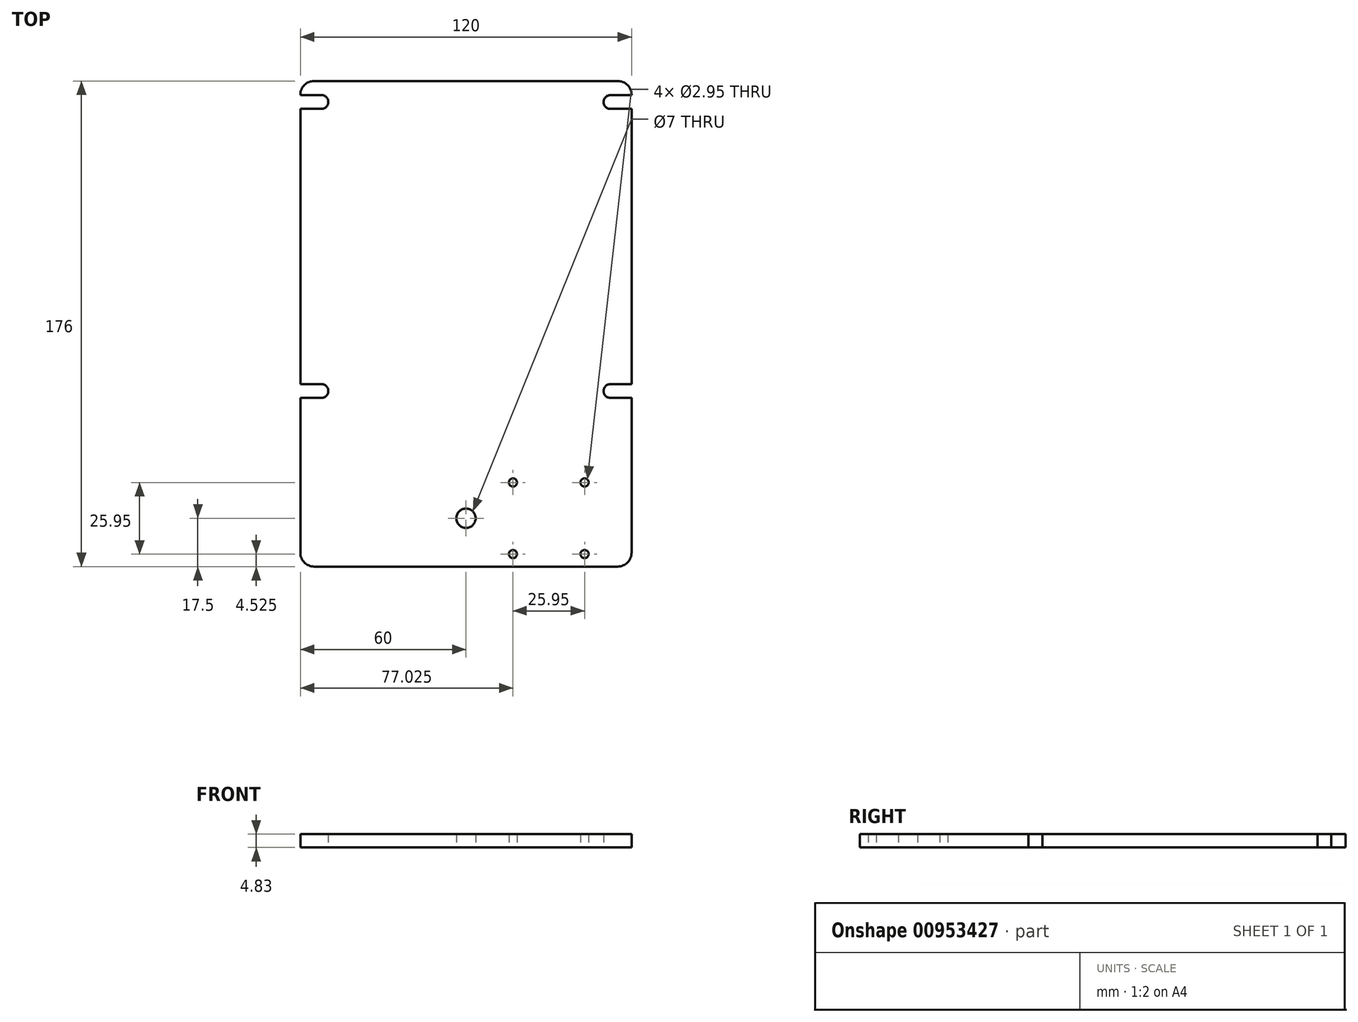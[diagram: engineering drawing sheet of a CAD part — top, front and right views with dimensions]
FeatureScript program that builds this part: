
annotation { "Feature Type Name" : "Feature", "Feature Type Description" : "" }
export const myFeature = defineFeature(function(context is Context, id is Id, definition is map)
    precondition{}
    {
        {
            var Q0;
            Q0=qCreatedBy(makeId("Top.planeOp"),FACE);
            var sketch = newSketch(context, id + "F0", { "sketchPlane" : qUnion([Q0])});
            skLineSegment(sketch, "E0.bottom", {"start": v(60, -60) * mm, "end": v(-60, -60) * mm, "construction": true});
            skLineSegment(sketch, "E0.top", {"start": v(60, 60) * mm, "end": v(-60, 60) * mm});
            skLineSegment(sketch, "E0.left", {"start": v(60, -60) * mm, "end": v(60, 60) * mm});
            skLineSegment(sketch, "E0.right", {"start": v(-60, -60) * mm, "end": v(-60, 60) * mm});
            skPoint(sketch, "E0.middle", {"position": v(0, 0) * mm});
            skLineSegment(sketch, "E1", {"start": v(-60, 60) * mm, "end": v(60, -60) * mm, "construction": true});
            skCircle(sketch, "E2", {"center": v(-52.37, 52.37) * mm, "radius": 2 * mm});
            skLineSegment(sketch, "E3", {"start": v(-52.37, 54.37) * mm, "end": v(-52.37, 50.38) * mm, "construction": true});
            skLineSegment(sketch, "E4", {"start": v(-54.37, 52.37) * mm, "end": v(-50.37, 52.37) * mm, "construction": true});
            skCircle(sketch, "E5.1.0", {"center": v(-52.37, -52.37) * mm, "radius": 2 * mm});
            skLineSegment(sketch, "E5.1.1", {"start": v(-52.37, -54.37) * mm, "end": v(-52.37, -50.37) * mm, "construction": true});
            skLineSegment(sketch, "E5.1.2", {"start": v(-54.37, -52.37) * mm, "end": v(-50.38, -52.37) * mm, "construction": true});
            skCircle(sketch, "E5.2.0", {"center": v(52.37, -52.37) * mm, "radius": 2 * mm});
            skLineSegment(sketch, "E5.2.1", {"start": v(54.37, -52.37) * mm, "end": v(50.37, -52.37) * mm, "construction": true});
            skLineSegment(sketch, "E5.2.2", {"start": v(52.37, -54.37) * mm, "end": v(52.37, -50.38) * mm, "construction": true});
            skCircle(sketch, "E5.3.0", {"center": v(52.37, 52.37) * mm, "radius": 2 * mm});
            skLineSegment(sketch, "E5.3.1", {"start": v(52.37, 54.37) * mm, "end": v(52.37, 50.37) * mm, "construction": true});
            skLineSegment(sketch, "E5.3.2", {"start": v(54.37, 52.37) * mm, "end": v(50.38, 52.37) * mm, "construction": true});
            skLineSegment(sketch, "E6", {"start": v(60, -75) * mm, "end": v(-60, -75) * mm, "construction": true});
            skLineSegment(sketch, "E7", {"start": v(60, -81) * mm, "end": v(-60, -81) * mm, "construction": true});
            skLineSegment(sketch, "E8", {"start": v(-60, -116) * mm, "end": v(60, -116) * mm, "construction": true});
            skLineSegment(sketch, "E9", {"start": v(-60, -60) * mm, "end": v(-60, -116) * mm});
            skLineSegment(sketch, "E10", {"start": v(-60, -116) * mm, "end": v(60, -116) * mm});
            skLineSegment(sketch, "E11", {"start": v(60, -116) * mm, "end": v(60, -60) * mm});
            skCircle(sketch, "E12", {"center": v(0, 0) * mm, "radius": 19.75 * mm, "construction": true});
            skCircle(sketch, "E13", {"center": v(0, 0) * mm, "radius": 58.1 * mm, "construction": true});
            skSolve(sketch);
        }
        {
            var Q0;
            Q0=makeQuery(id+"F0.imprint","IMPRINT",FACE,{"disambiguationData":[TD([[makeQuery(id+"F0.imprint","IMPRINT",EDGE,{"derivedFrom":sQuery(id+"F0.wireOp",EDGE,"E0.top")}),1.0]])]});
            var sketch = newSketch(context, id + "F1", { "sketchPlane" : qUnion([Q0])});
            skLineSegment(sketch, "E14.0", {"start": v(60, 60) * mm, "end": v(-60, 60) * mm});
            skLineSegment(sketch, "E15.0", {"start": v(-60, -60) * mm, "end": v(-60, 60) * mm});
            skLineSegment(sketch, "E16.0", {"start": v(60, -60) * mm, "end": v(60, 60) * mm});
            skLineSegment(sketch, "E17.0", {"start": v(60, -116) * mm, "end": v(60, -60) * mm});
            skLineSegment(sketch, "E18.0", {"start": v(-60, -60) * mm, "end": v(-60, -116) * mm});
            skLineSegment(sketch, "E19.0", {"start": v(-60, -116) * mm, "end": v(60, -116) * mm});
            skLineSegment(sketch, "E20.0", {"start": v(60, -81) * mm, "end": v(-60, -81) * mm, "construction": true});
            skCircle(sketch, "E21.0", {"center": v(52.37, -52.37) * mm, "radius": 2 * mm, "construction": true});
            skCircle(sketch, "E22.0", {"center": v(-52.37, -52.37) * mm, "radius": 2 * mm, "construction": true});
            skCircle(sketch, "E23.0", {"center": v(52.37, 52.37) * mm, "radius": 2 * mm, "construction": true});
            skCircle(sketch, "E24.0", {"center": v(-52.37, 52.37) * mm, "radius": 2 * mm, "construction": true});
            skLineSegment(sketch, "E25.bottom", {"start": v(-14, -114.5) * mm, "end": v(-46, -114.5) * mm, "construction": true});
            skLineSegment(sketch, "E25.top", {"start": v(-14, -82.5) * mm, "end": v(-46, -82.5) * mm, "construction": true});
            skLineSegment(sketch, "E25.left", {"start": v(-14, -114.5) * mm, "end": v(-14, -82.5) * mm, "construction": true});
            skLineSegment(sketch, "E25.right", {"start": v(-46, -114.5) * mm, "end": v(-46, -82.5) * mm, "construction": true});
            skPoint(sketch, "E25.middle", {"position": v(-30, -98.5) * mm});
            skCircle(sketch, "E26", {"center": v(0, -98.5) * mm, "radius": 3.5 * mm});
            skLineSegment(sketch, "E27", {"start": v(0, -81) * mm, "end": v(0, -98.5) * mm, "construction": true});
            skLineSegment(sketch, "E28", {"start": v(0, -98.5) * mm, "end": v(0, -116) * mm, "construction": true});
            skLineSegment(sketch, "E29", {"start": v(0, -98.5) * mm, "end": v(-30, -98.5) * mm, "construction": true});
            skLineSegment(sketch, "E30", {"start": v(-30, -98.5) * mm, "end": v(-60, -98.5) * mm, "construction": true});
            skLineSegment(sketch, "E31.bottom", {"start": v(5.62, -103.25) * mm, "end": v(-5.63, -103.25) * mm, "construction": true});
            skLineSegment(sketch, "E31.top", {"start": v(5.62, -93.75) * mm, "end": v(-5.62, -93.75) * mm, "construction": true});
            skLineSegment(sketch, "E31.left", {"start": v(5.62, -103.25) * mm, "end": v(5.62, -93.75) * mm, "construction": true});
            skLineSegment(sketch, "E31.right", {"start": v(-5.63, -103.25) * mm, "end": v(-5.62, -93.75) * mm, "construction": true});
            skLineSegment(sketch, "E32", {"start": v(-14, -114.5) * mm, "end": v(-46, -82.5) * mm, "construction": true});
            skCircle(sketch, "E33", {"center": v(-42.98, -85.53) * mm, "radius": 1.43 * mm, "construction": true});
            skLineSegment(sketch, "E34", {"start": v(-41.55, -85.53) * mm, "end": v(-44.4, -85.53) * mm, "construction": true});
            skLineSegment(sketch, "E35", {"start": v(-42.98, -84.1) * mm, "end": v(-42.98, -86.95) * mm, "construction": true});
            skLineSegment(sketch, "E36.1.0", {"start": v(-44.4, -111.47) * mm, "end": v(-41.55, -111.47) * mm, "construction": true});
            skCircle(sketch, "E36.1.1", {"center": v(-42.98, -111.47) * mm, "radius": 1.43 * mm, "construction": true});
            skLineSegment(sketch, "E36.1.2", {"start": v(-42.98, -110.05) * mm, "end": v(-42.98, -112.9) * mm, "construction": true});
            skLineSegment(sketch, "E36.2.0", {"start": v(-17.03, -112.9) * mm, "end": v(-17.03, -110.05) * mm, "construction": true});
            skCircle(sketch, "E36.2.1", {"center": v(-17.03, -111.48) * mm, "radius": 1.43 * mm, "construction": true});
            skLineSegment(sketch, "E36.2.2", {"start": v(-18.45, -111.48) * mm, "end": v(-15.6, -111.48) * mm, "construction": true});
            skLineSegment(sketch, "E36.3.0", {"start": v(-15.6, -85.52) * mm, "end": v(-18.45, -85.52) * mm, "construction": true});
            skCircle(sketch, "E36.3.1", {"center": v(-17.03, -85.52) * mm, "radius": 1.43 * mm, "construction": true});
            skLineSegment(sketch, "E36.3.2", {"start": v(-17.03, -86.95) * mm, "end": v(-17.03, -84.1) * mm, "construction": true});
            skLineSegment(sketch, "E37.MirrorCS", {"start": v(44.4, -111.47) * mm, "end": v(41.55, -111.47) * mm, "construction": true});
            skLineSegment(sketch, "E38.MirrorCS", {"start": v(14, -114.5) * mm, "end": v(46, -82.5) * mm, "construction": true});
            skLineSegment(sketch, "E39.MirrorCS", {"start": v(17.03, -86.95) * mm, "end": v(17.03, -84.1) * mm, "construction": true});
            skPoint(sketch, "E40.MirrorP", {"position": v(30, -98.5) * mm});
            skLineSegment(sketch, "E41.MirrorCS", {"start": v(14, -82.5) * mm, "end": v(46, -82.5) * mm, "construction": true});
            skCircle(sketch, "E42.MirrorC", {"center": v(42.98, -111.47) * mm, "radius": 1.43 * mm, "construction": true});
            skCircle(sketch, "E43.MirrorC", {"center": v(17.03, -111.48) * mm, "radius": 1.43 * mm, "construction": true});
            skLineSegment(sketch, "E44.MirrorCS", {"start": v(14, -114.5) * mm, "end": v(46, -114.5) * mm, "construction": true});
            skCircle(sketch, "E45.MirrorC", {"center": v(42.98, -85.53) * mm, "radius": 1.43 * mm, "construction": true});
            skLineSegment(sketch, "E46.MirrorCS", {"start": v(18.45, -111.48) * mm, "end": v(15.6, -111.48) * mm, "construction": true});
            skLineSegment(sketch, "E47.MirrorCS", {"start": v(42.98, -110.05) * mm, "end": v(42.98, -112.9) * mm, "construction": true});
            skLineSegment(sketch, "E48.MirrorCS", {"start": v(46, -114.5) * mm, "end": v(46, -82.5) * mm, "construction": true});
            skLineSegment(sketch, "E49.MirrorCS", {"start": v(41.55, -85.53) * mm, "end": v(44.4, -85.53) * mm, "construction": true});
            skLineSegment(sketch, "E50.MirrorCS", {"start": v(14, -114.5) * mm, "end": v(14, -82.5) * mm, "construction": true});
            skLineSegment(sketch, "E51.MirrorCS", {"start": v(15.6, -85.52) * mm, "end": v(18.45, -85.52) * mm, "construction": true});
            skLineSegment(sketch, "E52.MirrorCS", {"start": v(17.03, -112.9) * mm, "end": v(17.03, -110.05) * mm, "construction": true});
            skLineSegment(sketch, "E53.MirrorCS", {"start": v(42.98, -84.1) * mm, "end": v(42.98, -86.95) * mm, "construction": true});
            skCircle(sketch, "E54.MirrorC", {"center": v(17.03, -85.52) * mm, "radius": 1.43 * mm, "construction": true});
            skCircle(sketch, "E55", {"center": v(42.98, -85.53) * mm, "radius": 1.47 * mm});
            skCircle(sketch, "E56.1.0", {"center": v(17.03, -85.53) * mm, "radius": 1.47 * mm});
            skCircle(sketch, "E56.2.0", {"center": v(17.03, -111.48) * mm, "radius": 1.47 * mm});
            skCircle(sketch, "E56.3.0", {"center": v(42.98, -111.48) * mm, "radius": 1.47 * mm});
            skCircle(sketch, "E57", {"center": v(-52.37, 52.37) * mm, "radius": 2.5 * mm});
            skLineSegment(sketch, "E58", {"start": v(-52.37, 54.87) * mm, "end": v(-60, 54.87) * mm});
            skLineSegment(sketch, "E59", {"start": v(-52.37, 49.87) * mm, "end": v(-60, 49.87) * mm});
            skLineSegment(sketch, "E60.MirrorCS", {"start": v(52.37, 54.87) * mm, "end": v(60, 54.87) * mm});
            skLineSegment(sketch, "E61.MirrorCS", {"start": v(52.37, 49.87) * mm, "end": v(60, 49.87) * mm});
            skCircle(sketch, "E62.MirrorC", {"center": v(52.37, 52.37) * mm, "radius": 2.5 * mm});
            skLineSegment(sketch, "E63.MirrorCS", {"start": v(52.37, -54.87) * mm, "end": v(60, -54.87) * mm});
            skCircle(sketch, "E64.MirrorC", {"center": v(-52.37, -52.37) * mm, "radius": 2.5 * mm});
            skCircle(sketch, "E65.MirrorC", {"center": v(52.37, -52.37) * mm, "radius": 2.5 * mm});
            skLineSegment(sketch, "E66.MirrorCS", {"start": v(-52.37, -49.87) * mm, "end": v(-60, -49.87) * mm});
            skLineSegment(sketch, "E67.MirrorCS", {"start": v(52.37, -49.87) * mm, "end": v(60, -49.87) * mm});
            skLineSegment(sketch, "E68.MirrorCS", {"start": v(-52.37, -54.87) * mm, "end": v(-60, -54.87) * mm});
            skSolve(sketch);
        }
        {
            var Q0;
            {var subQ11=sQuery(id+"F1.wireOp",EDGE,"E14.0");Q0=makeQuery(id+"F1.imprint","IMPRINT",FACE,{"disambiguationData":[TD([[makeQuery(id+"F1.imprint","IMPRINT",EDGE,{"derivedFrom":subQ11}),1.0]])]});}
            extrude(context, id + "F2", {"entities" : qUnion([Q0]), "depth" : 4.83 * mm, "offsetDistance" : 25.4 * mm});
        }
        {
            var Q0;
            Q0=makeQuery(id+"F2.opExtrude","SWEPT_EDGE",EDGE,{"disambiguationData":[OSD([sQuery(id+"F1.wireOp",EDGE,"E14.0"),sQuery(id+"F1.wireOp",EDGE,"E15.0")])]});
            var Q1;
            Q1=makeQuery(id+"F2.opExtrude","SWEPT_EDGE",EDGE,{"disambiguationData":[OSD([sQuery(id+"F1.wireOp",EDGE,"E14.0"),sQuery(id+"F1.wireOp",EDGE,"E16.0")])]});
            var Q2;
            Q2=makeQuery(id+"F2.opExtrude","SWEPT_EDGE",EDGE,{"disambiguationData":[OSD([sQuery(id+"F1.wireOp",EDGE,"E17.0"),sQuery(id+"F1.wireOp",EDGE,"E19.0")])]});
            var Q3;
            Q3=makeQuery(id+"F2.opExtrude","SWEPT_EDGE",EDGE,{"disambiguationData":[OSD([sQuery(id+"F1.wireOp",EDGE,"E18.0"),sQuery(id+"F1.wireOp",EDGE,"E19.0")])]});
            fillet(context, id + "F3", {"entities" : qUnion([Q0, Q1, Q2, Q3]), "radius" : 5 * mm, "tangentPropagation" : true, "allowEdgeOverflow" : false});
        }
    });
